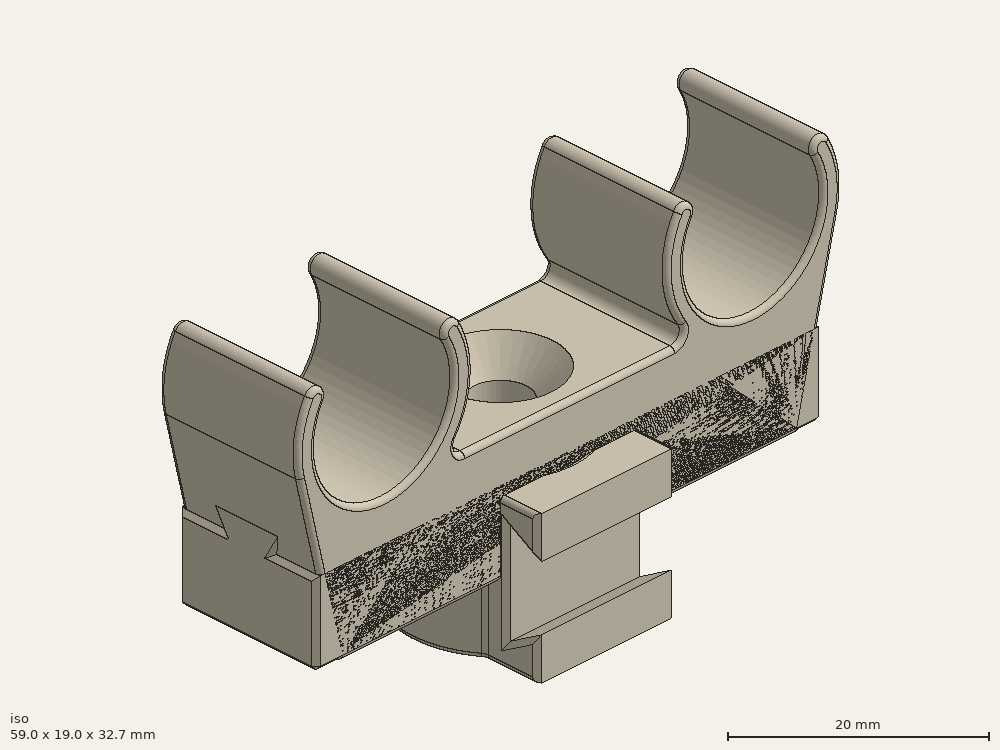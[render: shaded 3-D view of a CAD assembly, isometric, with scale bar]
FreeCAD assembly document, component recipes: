
FREECAD ASSEMBLY — COMPONENT RECIPES ("PipeMount")

This assembly document has 4 components, labeled P0..P3 below (a component is one placed body or linked part). 3 of them carry a construction recipe — the FreeCAD feature program that regenerates the part from scratch, quoted from this document or its linked companion documents; the rest are supplied as boundary geometry only. No exploded tour is included for this assembly.
COMPONENT P0 — geometry summary ("Assembly"; no construction recipe available for this part):
  bounding box: 59.0 x 25.2 x 15.0 mm
  tessellated surface: 62,380 triangles
  volume: 10180 mm^3 (46% of its bounding box)
  symmetry: 2-fold rotationally symmetric about the z axis; mirror-symmetric across its x mid-plane, y mid-plane
COMPONENT P1 — recipe-attached ("Double Mount", modeled in this document).
Construction recipe (the document's own serialized feature program — sketch geometry with constraints, then the solid features built on it; lengths are millimeters unless a unit is written):

FEATURE [Sketcher::SketchObject] Sketch
  ArcFitTolerance = 1e-06
  AttachmentSupport = -> [XZ_Plane]
  FullyConstrained = true
  MakeInternals = false
  MapMode = 5
  Placement = pos=(0,0,0) rot=(1,0,0;1.5708rad)
  expr: Constraints[35] = <<Spreadsheet>>.PipeDiameter
  expr: Constraints[36] = <<Spreadsheet>>.HolderThickness
  expr: Constraints[37] = <<Spreadsheet>>.PipeOpening
  expr: Constraints[38] = <<Spreadsheet>>.PipeDistance
  expr: Constraints[39] = <<Spreadsheet>>.WallDistance
  expr: Constraints[40] = <<Spreadsheet>>.FootLength
  expr: Constraints[41] = <<Spreadsheet>>.PipeCenterToFoot
  sketch-geometry (16):
    g0: ArcOfCircle CenterX=-20 CenterY=20 CenterZ=0 NormalX=0 NormalY=0 NormalZ=1 AngleXU=0 Radius=7.5 StartAngle=2.61928 EndAngle=6.8055
    g1: ArcOfCircle CenterX=20 CenterY=20 CenterZ=0 NormalX=0 NormalY=0 NormalZ=1 AngleXU=0 Radius=7.5 StartAngle=2.61928 EndAngle=6.8055
    g2: ArcOfCircle CenterX=-20 CenterY=20 CenterZ=0 NormalX=0 NormalY=0 NormalZ=1 AngleXU=0 Radius=9.5 StartAngle=2.61928 EndAngle=3.37553
    g3: ArcOfCircle CenterX=-20 CenterY=20 CenterZ=0 NormalX=0 NormalY=0 NormalZ=1 AngleXU=0 Radius=9.5 StartAngle=5.67494 EndAngle=6.8055
    g4: ArcOfCircle CenterX=20 CenterY=20 CenterZ=0 NormalX=0 NormalY=0 NormalZ=1 AngleXU=0 Radius=9.5 StartAngle=2.61928 EndAngle=3.74984
    g5: ArcOfCircle CenterX=20 CenterY=20 CenterZ=0 NormalX=0 NormalY=0 NormalZ=1 AngleXU=0 Radius=9.5 StartAngle=6.04925 EndAngle=6.8055
    g6: ArcOfCircle CenterX=-27.3667 CenterY=24.2405 CenterZ=0 NormalX=0 NormalY=0 NormalZ=1 AngleXU=0 Radius=1 StartAngle=5.76087 EndAngle=8.90246
    g7: ArcOfCircle CenterX=-12.6333 CenterY=24.2405 CenterZ=0 NormalX=0 NormalY=0 NormalZ=1 AngleXU=0 Radius=1 StartAngle=0.522315 EndAngle=3.66391
    g8: ArcOfCircle CenterX=12.6333 CenterY=24.2405 CenterZ=0 NormalX=0 NormalY=0 NormalZ=1 AngleXU=0 Radius=1 StartAngle=5.76087 EndAngle=8.90246
    g9: ArcOfCircle CenterX=27.3667 CenterY=24.2405 CenterZ=0 NormalX=0 NormalY=0 NormalZ=1 AngleXU=0 Radius=1 StartAngle=0.522315 EndAngle=3.66391
    g10: LineSegment StartX=-29.2412 StartY=17.7978 StartZ=0 EndX=-25 EndY=0 EndZ=0
    g11: LineSegment StartX=-25 StartY=0 StartZ=0 EndX=25 EndY=0 EndZ=0
    g12: LineSegment StartX=25 StartY=0 StartZ=0 EndX=29.2412 EndY=17.7978 EndZ=0
    g13: LineSegment StartX=-11.3832 StartY=13 StartZ=0 EndX=11.3832 EndY=13 EndZ=0
    g14: ArcOfCircle CenterX=11.3832 CenterY=14 CenterZ=0 NormalX=0 NormalY=0 NormalZ=1 AngleXU=0 Radius=1 StartAngle=4.71239 EndAngle=6.89143
    g15: ArcOfCircle CenterX=-11.3832 CenterY=14 CenterZ=0 NormalX=0 NormalY=0 NormalZ=1 AngleXU=0 Radius=1 StartAngle=2.53335 EndAngle=4.71239
  constraints (42):
    c: Symmetric(g1,g0,g-2)
    c: Equal(g0,g1)
    c: Horizontal(g0,g0)
    c: Horizontal(g0,g1)
    c: Horizontal(g1,g1)
    c: Coincident(g5,g1)
    c: Coincident(g5,g4)
    c: Coincident(g2,g0)
    c: Coincident(g2,g3)
    c: Equal(g2,g3)
    c: Equal(g3,g4)
    c: Equal(g4,g5)
    c: Tangent(g6,g0) = 1.5708
    c: Tangent(g6,g2) = -1.5708
    c: Tangent(g7,g0) = 1.5708
    c: Tangent(g7,g3) = -1.5708
    c: Tangent(g8,g4) = -1.5708
    c: Tangent(g8,g1) = 1.5708
    c: Tangent(g9,g1) = 1.5708
    c: Tangent(g9,g5) = -1.5708
    c: Horizontal(g2,g5)
    c: Tangent(g2,g10) = -1.5708
    c: Coincident(g10,g11)
    c: Horizontal(g11)
    c: Coincident(g11,g12)
    c: Tangent(g12,g5) = -1.5708
    c: PointOnObject(g-1,g11)
    c: Horizontal(g4,g3)
    c: Horizontal(g13)
    c: Tangent(g15,g13) = -1.5708
    c: Tangent(g15,g3) = 1.5708
    c: Tangent(g14,g13) = -1.5708
    c: Tangent(g14,g4) = 1.5708
    c: Equal(g15,g7)
    c: DistanceY(g-1,g13) = 13  'BottomThickness'
    c: Diameter(g1) = 15
    c: Diameter(g9) = 2
    c: DistanceX(g1,g1) = 13
    c: DistanceX(g0,g1) = 40
    c: DistanceY(g0) = 20
    c: DistanceX(g11,g11) = 50
    c: DistanceY(g13,g1) = 7
FEATURE [PartDesign::Pad] Pad
  Direction = (0,-1,2e-16)
  Length = 15
  Length2 = 10
  Midplane = true
  Placement = pos=(0,0,0) rot=(1,0,0;1.5708rad)
  Profile = -> Sketch
  ReferenceAxis = -> Sketch [N_Axis]
  Refine = true
  Suppressed = false
  Type = 0
  expr: Length = <<Spreadsheet>>.FootWidth
FEATURE [Sketcher::SketchObject] Sketch001
  ArcFitTolerance = 1e-06
  AttachmentSupport = -> [Pad]
  FullyConstrained = true
  MakeInternals = false
  MapMode = 5
  Placement = pos=(0,2.9e-15,13) rot=(0,0,1;3.14159rad)
  expr: Constraints[1] = <<Spreadsheet>>.HoleDiameter
  sketch-geometry (1):
    g0: Circle CenterX=0 CenterY=0 CenterZ=0 NormalX=0 NormalY=0 NormalZ=1 AngleXU=0 Radius=2.75
  constraints (2):
    c: Coincident(g0,g-1)
    c: Diameter(g0) = 5.5
FEATURE [PartDesign::Hole] Hole
  BaseFeature = -> Pad
  CustomThreadClearance = 0
  Depth = 129.413
  DepthType = 1
  Diameter = 5.5
  DrillForDepth = false
  DrillPoint = 1
  DrillPointAngle = 118
  HoleCutCountersinkAngle = 90
  HoleCutCustomValues = false
  HoleCutDepth = 1
  HoleCutDiameter = 11.2
  HoleCutType = 2
  ModelThread = false
  Placement = pos=(0,0,0) rot=(1,0,0;1.5708rad)
  Profile = -> Sketch001
  Refine = true
  Suppressed = false
  Tapered = false
  TaperedAngle = 90
  ThreadClass = 0
  ThreadDepth = 129.413
  ThreadDepthType = 0
  ThreadDirection = 0
  ThreadFit = 0
  ThreadSize = 0
  ThreadType = 0
  Threaded = false
  UseCustomThreadClearance = false
  expr: Diameter = <<Spreadsheet>>.HoleDiameter
  expr: HoleCutDepth = <<Spreadsheet>>.HeadDepth
  expr: HoleCutDiameter = <<Spreadsheet>>.HeadDiameter
FEATURE [PartDesign::Fillet] Fillet001
  Base = -> Hole [Face18,Edge21,Edge34]
  BaseFeature = -> Hole
  Placement = pos=(0,0,0) rot=(1,0,0;1.5708rad)
  Radius = 0.5
  Refine = true
  SupportTransform = false
  Suppressed = false
  UseAllEdges = false
FEATURE [PartDesign::Body] Body  label="Double Mount"
  AllowCompound = false
  Group = -> [Sketch,Pad,Sketch001,Hole,Fillet001]
  Origin = -> Origin
  Tip = -> Fillet001
COMPONENT P2 — recipe-attached ("Modular - Pipe Holder", modeled in this document).
Construction recipe (the document's own serialized feature program — sketch geometry with constraints, then the solid features built on it; lengths are millimeters unless a unit is written):

FEATURE [Sketcher::SketchObject] Sketch002
  ArcFitTolerance = 1e-06
  AttachmentSupport = -> [XY_Plane001]
  FullyConstrained = true
  MakeInternals = false
  MapMode = 5
  expr: Constraints[10] = <<Spreadsheet>>.PipeDiameter
  expr: Constraints[11] = <<Spreadsheet>>.HolderThickness
  expr: Constraints[12] = <<Spreadsheet>>.PipeOpening
  expr: Constraints[25] = <<Spreadsheet>>.ModularPipeHolderBaseLength
  expr: Constraints[28] = <<Spreadsheet>>.ModularPipeHolderBaseThickness + <<Spreadsheet>>.WedgeHeight
  expr: Constraints[37] = <<Spreadsheet>>.ModularBaseHeight
  sketch-geometry (14):
    g0: ArcOfCircle CenterX=0 CenterY=0 CenterZ=0 NormalX=0 NormalY=0 NormalZ=1 AngleXU=0 Radius=7.5 StartAngle=2.61928 EndAngle=6.8055
    g1: ArcOfCircle CenterX=0 CenterY=0 CenterZ=0 NormalX=0 NormalY=0 NormalZ=1 AngleXU=0 Radius=9.5 StartAngle=2.61928 EndAngle=3.76905
    g2: ArcOfCircle CenterX=0 CenterY=0 CenterZ=0 NormalX=0 NormalY=0 NormalZ=1 AngleXU=0 Radius=9.5 StartAngle=5.65573 EndAngle=6.8055
    g3: ArcOfCircle CenterX=-7.36667 CenterY=4.24055 CenterZ=0 NormalX=0 NormalY=0 NormalZ=1 AngleXU=0 Radius=1 StartAngle=5.76087 EndAngle=8.90246
    g4: ArcOfCircle CenterX=7.36667 CenterY=4.24055 CenterZ=0 NormalX=0 NormalY=0 NormalZ=1 AngleXU=0 Radius=1 StartAngle=0.522315 EndAngle=3.66391
    g5: ArcOfCircle CenterX=-8.5 CenterY=-6.16441 CenterZ=0 NormalX=0 NormalY=0 NormalZ=1 AngleXU=0 Radius=1 StartAngle=2e-16 EndAngle=0.627456
    g6: ArcOfCircle CenterX=8.5 CenterY=-6.16441 CenterZ=0 NormalX=0 NormalY=0 NormalZ=1 AngleXU=0 Radius=1 StartAngle=2.51414 EndAngle=3.14159
    g7: LineSegment StartX=-7.5 StartY=-6.16441 StartZ=0 EndX=-7.5 EndY=-11.5 EndZ=0
    g8: LineSegment StartX=-7.5 StartY=-11.5 StartZ=0 EndX=7.5 EndY=-11.5 EndZ=0
    g9: LineSegment StartX=7.5 StartY=-11.5 StartZ=0 EndX=7.5 EndY=-6.16441 EndZ=0
    g10: GeomPoint X=0 Y=-7.5 Z=0
    g11: LineSegment [constr] StartX=-7.5 StartY=-11.5 StartZ=0 EndX=-7.5 EndY=-20 EndZ=0
    g12: LineSegment [constr] StartX=-7.5 StartY=-20 StartZ=0 EndX=7.5 EndY=-20 EndZ=0
    g13: LineSegment [constr] StartX=7.5 StartY=-20 StartZ=0 EndX=7.5 EndY=-11.5 EndZ=0
  constraints (39):
    c: Tangent(g3,g1) = -1.5708
    c: Tangent(g3,g0) = 1.5708
    c: Tangent(g4,g0) = 1.5708
    c: Coincident(g1,g0)
    c: Coincident(g1,g2)
    c: Coincident(g1,g-1)
    c: Tangent(g4,g2) = -1.5708
    c: Equal(g1,g2)
    c: Horizontal(g0,g0)
    c: Horizontal(g1,g2)
    c: Diameter(g0) = 15
    c: Diameter(g4) = 2
    c: DistanceX(g0,g0) = 13
    c: Coincident(g5,g1)
    c: Tangent(g5,g7) = 1.5708
    c: Coincident(g7,g8)
    c: Horizontal(g8)
    c: Coincident(g8,g9)
    c: Vertical(g9)
    c: Tangent(g9,g6) = 1.5708
    c: Tangent(g6,g2) = 1.5708
    c: Vertical(g7)
    c: Equal(g9,g7)
    c: Equal(g5,g6)
    c: Equal(g6,g4)
    c: DistanceX(g8,g8) = 15
    c: PointOnObject(g10,g0)
    c: PointOnObject(g10,g-2)
    c: DistanceY(g8,g10) = 4
    c: Coincident(g7,g11)
    c: Vertical(g11)
    c: Coincident(g11,g12)
    c: Horizontal(g12)
    c: Coincident(g12,g13)
    c: Coincident(g13,g8)
    c: Vertical(g13)
    c: DistanceY(g11,g0) = 20
    c: DistanceY(g13,g13) = 8.5
    c: DistanceY(g7,g-1) = 11.5
FEATURE [PartDesign::Pad] Pad001
  Direction = (0,0,1)
  Length = 15
  Length2 = 10
  Midplane = true
  Profile = -> Sketch002
  ReferenceAxis = -> Sketch002 [N_Axis]
  Refine = true
  Suppressed = false
  Type = 0
  expr: Length = <<Spreadsheet>>.FootWidth
FEATURE [Sketcher::SketchObject] Sketch003
  ArcFitTolerance = 1e-06
  AttachmentSupport = -> [Pad001]
  ExternalGeometry = -> [Pad001]
  FullyConstrained = true
  MakeInternals = false
  MapMode = 5
  Placement = pos=(7.5,0,0) rot=(0.57735,0.57735,0.57735;2.0944rad)
  expr: Constraints[10] = <<Spreadsheet>>.WedgeAngle
  expr: Constraints[6] = <<Spreadsheet>>.WedgeWidth + <<Spreadsheet>>.WedgeTolerance
  expr: Constraints[7] = <<Spreadsheet>>.WedgeHeight + <<Spreadsheet>>.WedgeTolerance
  sketch-geometry (4):
    g0: LineSegment StartX=-11.5 StartY=-3.23701 StartZ=0 EndX=-11.5 EndY=3.23701 EndZ=0
    g1: LineSegment StartX=-11.5 StartY=3.23701 StartZ=0 EndX=-8.1 EndY=5.2 EndZ=0
    g2: LineSegment StartX=-8.1 StartY=5.2 StartZ=0 EndX=-8.1 EndY=-5.2 EndZ=0
    g3: LineSegment StartX=-8.1 StartY=-5.2 StartZ=0 EndX=-11.5 EndY=-3.23701 EndZ=0
  constraints (11):
    c: Coincident(g0,g1)
    c: Coincident(g1,g2)
    c: Coincident(g2,g3)
    c: Coincident(g3,g0)
    c: Symmetric(g0,g0,g-1)
    c: Symmetric(g2,g1,g-1)
    c: DistanceY(g2,g2) = 10.4
    c: DistanceX(g0,g1) = 3.4
    c: PointOnObject(g0,g-3)
    c: DistanceY(g0,g0) = 6.47402
    c: Angle(g1,g2) = 1.0472
FEATURE [PartDesign::Pocket] Pocket
  BaseFeature = -> Pad001
  Direction = (-1,0,0)
  Length = 5
  Length2 = 5
  Profile = -> Sketch003
  ReferenceAxis = -> Sketch003 [N_Axis]
  Refine = true
  Suppressed = false
  Type = 1
FEATURE [PartDesign::CoordinateSystem] Mount_Center  label="Mount Center"
  AttacherType = Attacher::AttachEngine3D
  AttachmentSupport = -> [Pocket]
  MapMode = 45
  Placement = pos=(-9e-16,-11.5,0) rot=(0.57735,0.57735,0.57735;4.18879rad)
FEATURE [PartDesign::Chamfer] Chamfer002
  Angle = 45
  Base = -> Pocket [Edge29,Edge30,Edge31,Edge32,Edge33]
  BaseFeature = -> Pocket
  ChamferType = 0
  FlipDirection = false
  Refine = true
  Size = 0.5
  Size2 = 1
  SupportTransform = false
  Suppressed = false
  UseAllEdges = false
  expr: Size = Spreadsheet.FilletChamfer
FEATURE [PartDesign::Chamfer] Chamfer003
  Angle = 45
  Base = -> Chamfer002 [Edge23,Edge27,Edge28,Edge29,Edge30]
  BaseFeature = -> Chamfer002
  ChamferType = 0
  FlipDirection = false
  Refine = true
  Size = 0.5
  Size2 = 1
  SupportTransform = false
  Suppressed = false
  UseAllEdges = false
  expr: Size = <<Spreadsheet>>.FilletChamfer
FEATURE [PartDesign::Fillet] Fillet002
  Base = -> Chamfer003 [Edge11]
  BaseFeature = -> Chamfer003
  Radius = 0.5
  Refine = true
  SupportTransform = false
  Suppressed = false
  UseAllEdges = false
  expr: Radius = <<Spreadsheet>>.FilletChamfer
FEATURE [PartDesign::Fillet] Fillet003
  Base = -> Fillet002 [Edge58]
  BaseFeature = -> Fillet002
  Radius = 0.5
  Refine = true
  SupportTransform = false
  Suppressed = false
  UseAllEdges = false
  expr: Radius = <<Spreadsheet>>.FilletChamfer
FEATURE [PartDesign::Body] Body001  label="Modular - Pipe Holder"
  AllowCompound = false
  Group = -> [Sketch002,Pad001,Sketch003,Pocket,Mount_Center,Chamfer002,Chamfer003,Fillet002,Fillet003]
  Origin = -> Origin002
  Tip = -> Fillet003
COMPONENT P3 — recipe-attached ("Modular - Holder Base", modeled in this document).
Construction recipe (the document's own serialized feature program — sketch geometry with constraints, then the solid features built on it; lengths are millimeters unless a unit is written):

FEATURE [Sketcher::SketchObject] Sketch004
  ArcFitTolerance = 1e-06
  AttachmentSupport = -> [YZ_Plane002]
  FullyConstrained = true
  MakeInternals = false
  MapMode = 5
  Placement = pos=(0,0,0) rot=(0.57735,0.57735,0.57735;2.0944rad)
  expr: Constraints[17] = <<Spreadsheet>>.FootWidth
  expr: Constraints[18] = <<Spreadsheet>>.ModularBaseHeight
  expr: Constraints[25] = <<Spreadsheet>>.WedgeWidth
  expr: Constraints[26] = <<Spreadsheet>>.WedgeAngle
  expr: Constraints[27] = <<Spreadsheet>>.WedgeHeight
  expr: Constraints[28] = <<Spreadsheet>>.WedgeTolerance
  expr: Constraints[30] = <<Spreadsheet>>.WedgeTolerance
  sketch-geometry (11):
    g0: LineSegment StartX=-7.5 StartY=0 StartZ=0 EndX=7.5 EndY=0 EndZ=0
    g1: LineSegment StartX=7.5 StartY=0 StartZ=0 EndX=7.5 EndY=8.5 EndZ=0
    g2: LineSegment StartX=7.5 StartY=8.5 StartZ=0 EndX=2.80607 EndY=8.5 EndZ=0
    g3: LineSegment StartX=2.80607 StartY=8.5 StartZ=0 EndX=4.30718 EndY=11.1 EndZ=0
    g4: LineSegment StartX=4.30718 StartY=11.1 StartZ=0 EndX=-4.30718 EndY=11.1 EndZ=0
    g5: LineSegment StartX=-4.30718 StartY=11.1 StartZ=0 EndX=-2.80607 EndY=8.5 EndZ=0
    g6: LineSegment StartX=-2.80607 StartY=8.5 StartZ=0 EndX=-7.5 EndY=8.5 EndZ=0
    g7: LineSegment StartX=-7.5 StartY=8.5 StartZ=0 EndX=-7.5 EndY=0 EndZ=0
    g8: LineSegment [constr] StartX=-3.26795 StartY=8.5 StartZ=0 EndX=-5 EndY=11.5 EndZ=0
    g9: LineSegment [constr] StartX=-5 StartY=11.5 StartZ=0 EndX=5 EndY=11.5 EndZ=0
    g10: LineSegment [constr] StartX=5 StartY=11.5 StartZ=0 EndX=3.26795 EndY=8.5 EndZ=0
  constraints (31):
    c: PointOnObject(g0,g-1)
    c: Coincident(g0,g1)
    c: Vertical(g1)
    c: Coincident(g1,g2)
    c: Horizontal(g2)
    c: Coincident(g2,g3)
    c: Coincident(g3,g4)
    c: Coincident(g4,g5)
    c: Coincident(g5,g6)
    c: Coincident(g6,g7)
    c: Coincident(g7,g0)
    c: Vertical(g7)
    c: Horizontal(g6)
    c: Symmetric(g3,g4,g-2)
    c: Symmetric(g0,g0,g-2)
    c: Equal(g7,g1)
    c: Equal(g2,g6)
    c: DistanceX(g0,g0) = 15
    c: DistanceY(g7,g7) = 8.5
    c: DistanceX(g5,g2) = 5.61214
    c: PointOnObject(g8,g6)
    c: Coincident(g8,g9)
    c: Coincident(g9,g10)
    c: Symmetric(g9,g8,g-2)
    c: Symmetric(g10,g8,g-2)
    c: DistanceX(g9,g9) = 10
    c: Angle(g9,g10) = 1.0472
    c: DistanceY(g10,g9) = 3
    c: DistanceY(g3,g9) = 0.4
    c: Parallel(g3,g10)
    c: Distance(g3,g10) = 0.4
FEATURE [PartDesign::Pad] Pad002
  Direction = (1,0,0)
  Length = 55
  Length2 = 10
  Midplane = true
  Placement = pos=(0,0,0) rot=(1,1,1;2.0944rad)
  Profile = -> Sketch004
  ReferenceAxis = -> Sketch004 [N_Axis]
  Refine = true
  Suppressed = false
  Type = 0
  expr: Length = <<Spreadsheet>>.PipeDistance + <<Spreadsheet>>.PipeDiameter
FEATURE [Sketcher::SketchObject] Sketch005
  ArcFitTolerance = 1e-06
  AttachmentSupport = -> [Pad002]
  ExternalGeometry = -> [Pad002]
  FullyConstrained = true
  MakeInternals = false
  MapMode = 5
  Placement = pos=(-1.7e-15,-7.5,8e-16) rot=(0.57735,0.57735,-0.57735;2.0944rad)
  expr: Constraints[10] = <<Spreadsheet>>.BaseMaxHeight
  expr: Constraints[11] = <<Spreadsheet>>.ModularPipeHolderBaseLength
  sketch-geometry (5):
    g0: LineSegment StartX=-11.1 StartY=12.5 StartZ=0 EndX=-11.1 EndY=-12.5 EndZ=0
    g1: LineSegment StartX=-11.1 StartY=-12.5 StartZ=0 EndX=-10 EndY=-12.5 EndZ=0
    g2: LineSegment StartX=-10 StartY=-12.5 StartZ=0 EndX=-10 EndY=12.5 EndZ=0
    g3: LineSegment StartX=-10 StartY=12.5 StartZ=0 EndX=-11.1 EndY=12.5 EndZ=0
    g4: GeomPoint [constr] X=-10.55 Y=0 Z=0
  constraints (13):
    c: Coincident(g0,g1)
    c: Coincident(g1,g2)
    c: Coincident(g2,g3)
    c: Coincident(g3,g0)
    c: Vertical(g0)
    c: Vertical(g2)
    c: Horizontal(g1)
    c: Horizontal(g3)
    c: Symmetric(g2,g0,g4)
    c: PointOnObject(g4,g-1)
    c: DistanceX(g2,g-1) = 10
    c: DistanceY(g2,g-3) = 15
    c: PointOnObject(g0,g-4)
FEATURE [PartDesign::Pocket] Pocket001
  BaseFeature = -> Pad002
  Direction = (0,1,0)
  Length = 5
  Length2 = 5
  Placement = pos=(0,0,0) rot=(1,1,1;2.0944rad)
  Profile = -> Sketch005
  ReferenceAxis = -> Sketch005 [N_Axis]
  Refine = true
  Suppressed = false
  Type = 1
FEATURE [Sketcher::SketchObject] Sketch006
  ArcFitTolerance = 1e-06
  AttachmentSupport = -> [Pocket001]
  FullyConstrained = true
  MakeInternals = false
  MapMode = 5
  Placement = pos=(-1.1e-15,3.3e-15,10) rot=(0,0,-1;1.5708rad)
  expr: Constraints[1] = <<Spreadsheet>>.HoleDiameter
  sketch-geometry (1):
    g0: Circle CenterX=0 CenterY=0 CenterZ=0 NormalX=0 NormalY=0 NormalZ=1 AngleXU=0 Radius=2.75
  constraints (2):
    c: Coincident(g0,g-1)
    c: Diameter(g0) = 5.5
FEATURE [PartDesign::Hole] Hole001
  BaseFeature = -> Pocket001
  CustomThreadClearance = 0
  Depth = 25
  DepthType = 0
  Diameter = 6
  DrillForDepth = false
  DrillPoint = 1
  DrillPointAngle = 118
  HoleCutCountersinkAngle = 90
  HoleCutCustomValues = false
  HoleCutDepth = 1
  HoleCutDiameter = 11.2
  HoleCutType = 2
  ModelThread = false
  Placement = pos=(0,0,0) rot=(1,1,1;2.0944rad)
  Profile = -> Sketch006
  Refine = true
  Suppressed = false
  Tapered = false
  TaperedAngle = 90
  ThreadClass = 0
  ThreadDepth = 25
  ThreadDepthType = 0
  ThreadDirection = 0
  ThreadFit = 0
  ThreadSize = 0
  ThreadType = 0
  Threaded = false
  UseCustomThreadClearance = false
  expr: HoleCutDepth = <<Spreadsheet>>.HeadDepth
  expr: HoleCutDiameter = <<Spreadsheet>>.HeadDiameter
FEATURE [PartDesign::CoordinateSystem] Bottom_Center  label="Bottom Center"
  AttacherType = Attacher::AttachEngine3D
  AttachmentSupport = -> [Hole001]
  MapMode = 11
  Placement = pos=(-1.1e-15,3.6e-15,1.51e-14) rot=(1,0,0;3.14159rad)
FEATURE [PartDesign::CoordinateSystem] Holder_1  label="Holder 1"
  AttacherType = Attacher::AttachEngine3D
  AttachmentOffset = pos=(7.5,0,0) rot=(0,0,1;0rad)
  AttachmentSupport = -> [Hole001]
  MapMode = 45
  Placement = pos=(20,-1.59e-14,8.5) rot=(0,0.707107,0.707107;3.14159rad)
  expr: .AttachmentOffset.Base.x = <<Spreadsheet>>.ModularPipeHolderBaseLength / 2
FEATURE [PartDesign::CoordinateSystem] Holder_2  label="Holder 2"
  AttacherType = Attacher::AttachEngine3D
  AttachmentOffset = pos=(-7.5,0,0) rot=(0,0,1;0rad)
  AttachmentSupport = -> [Hole001]
  MapMode = 45
  Placement = pos=(-20,2.12e-14,8.5) rot=(0,0.707107,0.707107;3.14159rad)
  expr: .AttachmentOffset.Base.x = -<<Spreadsheet>>.ModularPipeHolderBaseLength / 2
FEATURE [PartDesign::Chamfer] Chamfer
  Angle = 45
  Base = -> Hole001 [Face4,Face1,Face3]
  BaseFeature = -> Hole001
  ChamferType = 0
  FlipDirection = false
  Placement = pos=(0,0,0) rot=(1,1,1;2.0944rad)
  Refine = true
  Size = 0.5
  Size2 = 1
  SupportTransform = false
  Suppressed = false
  UseAllEdges = false
  expr: Size = <<Spreadsheet>>.FilletChamfer
FEATURE [PartDesign::Body] Body002  label="Modular - Holder Base"
  AllowCompound = false
  Group = -> [Sketch004,Pad002,Bottom_Center,Holder_1,Holder_2,Sketch005,Pocket001,Sketch006,Hole001,Chamfer]
  Origin = -> Origin003
  Tip = -> Chamfer
PROVENANCE & LICENSES
A FreeCAD (.FCStd) document from a public repository crawl; recipes are the document's own serialized feature recipes (and, for linked parts, companion documents' recipes).
License: as declared in the source repository (recorded in the dataset sidecar).
